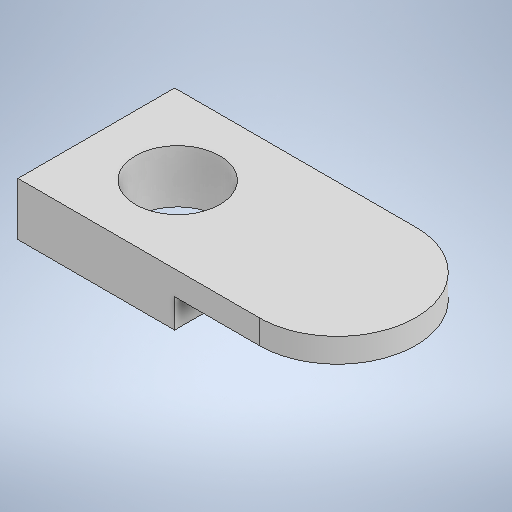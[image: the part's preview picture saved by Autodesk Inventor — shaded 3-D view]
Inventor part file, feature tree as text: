
AUTODESK INVENTOR PART (.ipt)
format: ipt  version: 2025 (Build 290162000, 162)  size: 230,400 bytes
history: native  units: in
note: dims shown in document units (in); Inventor stores cm internally (conversion verified against a paired STEP export)
features: extrude x3, sketch x3, projected_geometry x2
ambient origin geometry x8: Origin, YZ Plane, XZ Plane, XY Plane, X Axis, Y Axis, Z Axis, Center Point
bodies: Solid1 (feature_tree)
feature tree (8):
  extrude  "Extrusion1"  Depth=0.3937in
  extrude  "Extrusion2"  Depth=0.2559in
  extrude  "Extrusion3"  Depth=0.0472in
  sketch  "Sketch1"  dims[d1=0.2559in d2=0.3937in]
  sketch  "Sketch2"  dims[d3=0.0394in d4=0.0in d5=0.2559in]
  projected_geometry  "Projected Loop1"
  sketch  "Sketch3"  dims[d6=0.1329in d7=0.1378in d8=0.0394in d9=0.0in d10=0.2559in d11=0.0472in d12=0.0in]
  projected_geometry  "Projected Loop2"
